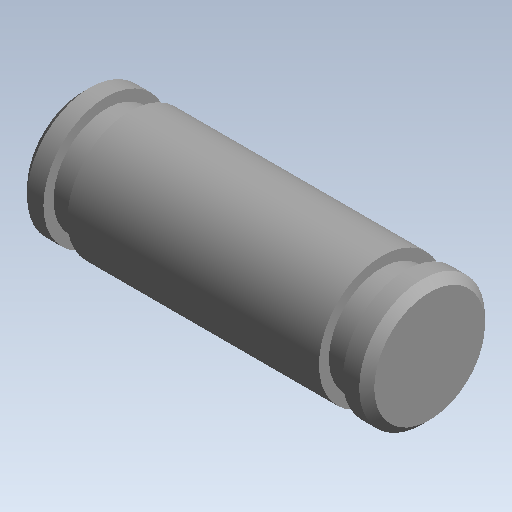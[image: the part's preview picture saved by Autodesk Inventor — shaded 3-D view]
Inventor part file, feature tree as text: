
AUTODESK INVENTOR PART (.ipt)
format: ipt  version: 2020 (Build 240168000, 168)  size: 126,464 bytes
history: native  units: mm (DEFAULTED — no unit token found)
features: other x49, revolve x1, sketch x1
ambient origin geometry x8: Origin, YZ Plane, XZ Plane, XY Plane, X Axis, Y Axis, Z Axis, Center Point
bodies: Solid1 (feature_tree)
feature tree (51):
  revolve  "Revolution1"  [1 undecoded]
  other  "p1_XY"
  other  "p1_YZ"
  other  "p1_ZX"
  other  "p1_X"
  other  "p1_Y"
  other  "p1_Z"
  other  "p1_Center"
  other  "p2_XY"
  other  "p2_YZ"
  other  "p2_ZX"
  other  "p2_X"
  other  "p2_Y"
  other  "p2_Z"
  other  "p2_Center"
  other  "pin_XY"
  other  "pin_YZ"
  other  "pin_ZX"
  other  "pin_X"
  other  "pin_Y"
  other  "pin_Z"
  other  "pin_Center"
  other  "rr1_XY"
  other  "rr1_YZ"
  other  "rr1_ZX"
  other  "rr1_X"
  other  "rr1_Y"
  other  "rr1_Z"
  other  "rr1_Center"
  other  "rr2_XY"
  other  "rr2_YZ"
  other  "rr2_ZX"
  other  "rr2_X"
  other  "rr2_Y"
  other  "rr2_Z"
  other  "rr2_Center"
  other  "w21_XY"
  other  "w21_YZ"
  other  "w21_ZX"
  other  "w21_X"
  other  "w21_Y"
  other  "w21_Z"
  other  "w21_Center"
  other  "w22_XY"
  other  "w22_YZ"
  other  "w22_ZX"
  other  "w22_X"
  other  "w22_Y"
  other  "w22_Z"
  other  "w22_Center"
  sketch  "Sketch_1"  dims[d0=360.0deg]
note: 1 required parameter value undecoded (feature->parameter linkage not recoverable at this tier; creation-order binding heuristic only, values carry confidence <= 0.55)
